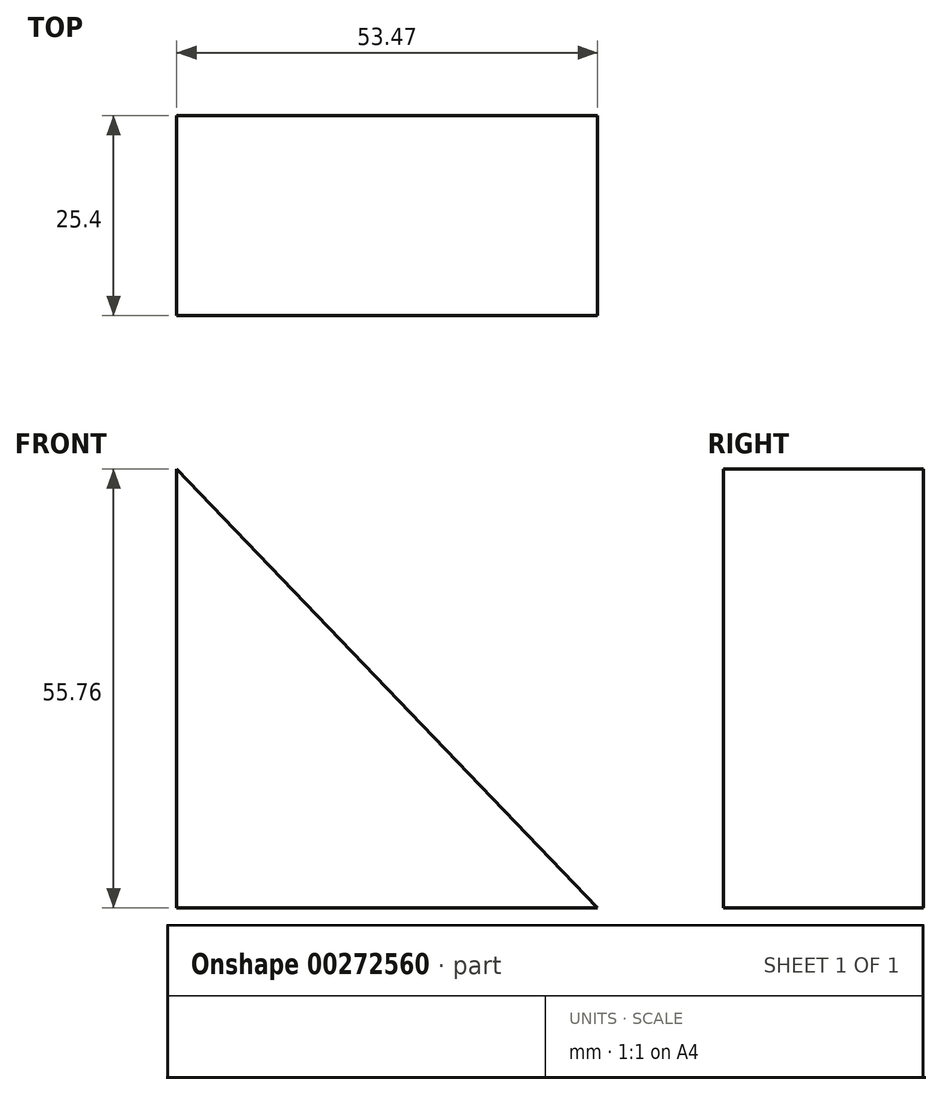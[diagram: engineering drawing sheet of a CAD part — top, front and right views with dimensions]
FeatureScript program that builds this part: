
annotation { "Feature Type Name" : "Feature", "Feature Type Description" : "" }
export const myFeature = defineFeature(function(context is Context, id is Id, definition is map)
    precondition{}
    {
        {
            var Q0;
            Q0=qCreatedBy(makeId("Front.planeOp"),FACE);
            var sketch = newSketch(context, id + "F0", { "sketchPlane" : qUnion([Q0])});
            skLineSegment(sketch, "E0", {"start": v(0, 0) * mm, "end": v(-53.47, 0) * mm});
            skLineSegment(sketch, "E1", {"start": v(-53.47, 0) * mm, "end": v(-53.47, 55.76) * mm});
            skLineSegment(sketch, "E2", {"start": v(-53.47, 55.76) * mm, "end": v(0, 0) * mm});
            skSolve(sketch);
        }
        {
            var Q0;
            Q0 = qSketchRegion(id + "F0", true);
            extrude(context, id + "F1", {"entities" : qUnion([Q0]), "depth" : 25.4 * mm});
        }
    });
